# Revit family: SEQ_A3-M-Electric-Lift-wall-based
name_source: partatom
category: Specialty Equipment
revit_build: Autodesk Revit 2016 (Build: 20150220_1215(x64)
units: mm (PartAtom-declared; Revit-internal decimal feet)

## family parameters
Always vertical = Yes
Cut with Voids When Loaded = No
Host = Wall
OmniClass Number = 23.50.05.14
OmniClass Title = Lifts
Part Type = Normal
Room Calculation Point = No
Round Connector Dimension = Use Diameter
Shared = No

## types (3) — shared parameters
Assembly Code = D1010
Door Material = <By Category>
Level Height = 3000 mm  [stored 9.84252 ft]
Manufacturer = Revit

## per-type parameters (varying)
| type | D1 | Length | Width |
| Lift 1300 x 950mm | 520 mm  [stored 1.70604 ft] | 1300 mm  [stored 4.26509 ft] | 950 mm  [stored 3.1168 ft] |
| Lift 1400 x 1100mm | 620 mm  [stored 2.03412 ft] | 1400 mm | 1100 mm |
| Lift 2100 x 1100mm | 1000 mm  [stored 3.28084 ft] | 2100 mm | 1100 mm |

note: [stored X ft] marks values corroborated as IEEE doubles in the binary element streams (Revit-internal decimal feet)

## geometry (parser evidence)
native form markers: Sweep x3
no freeform markers — native parametric forms only
